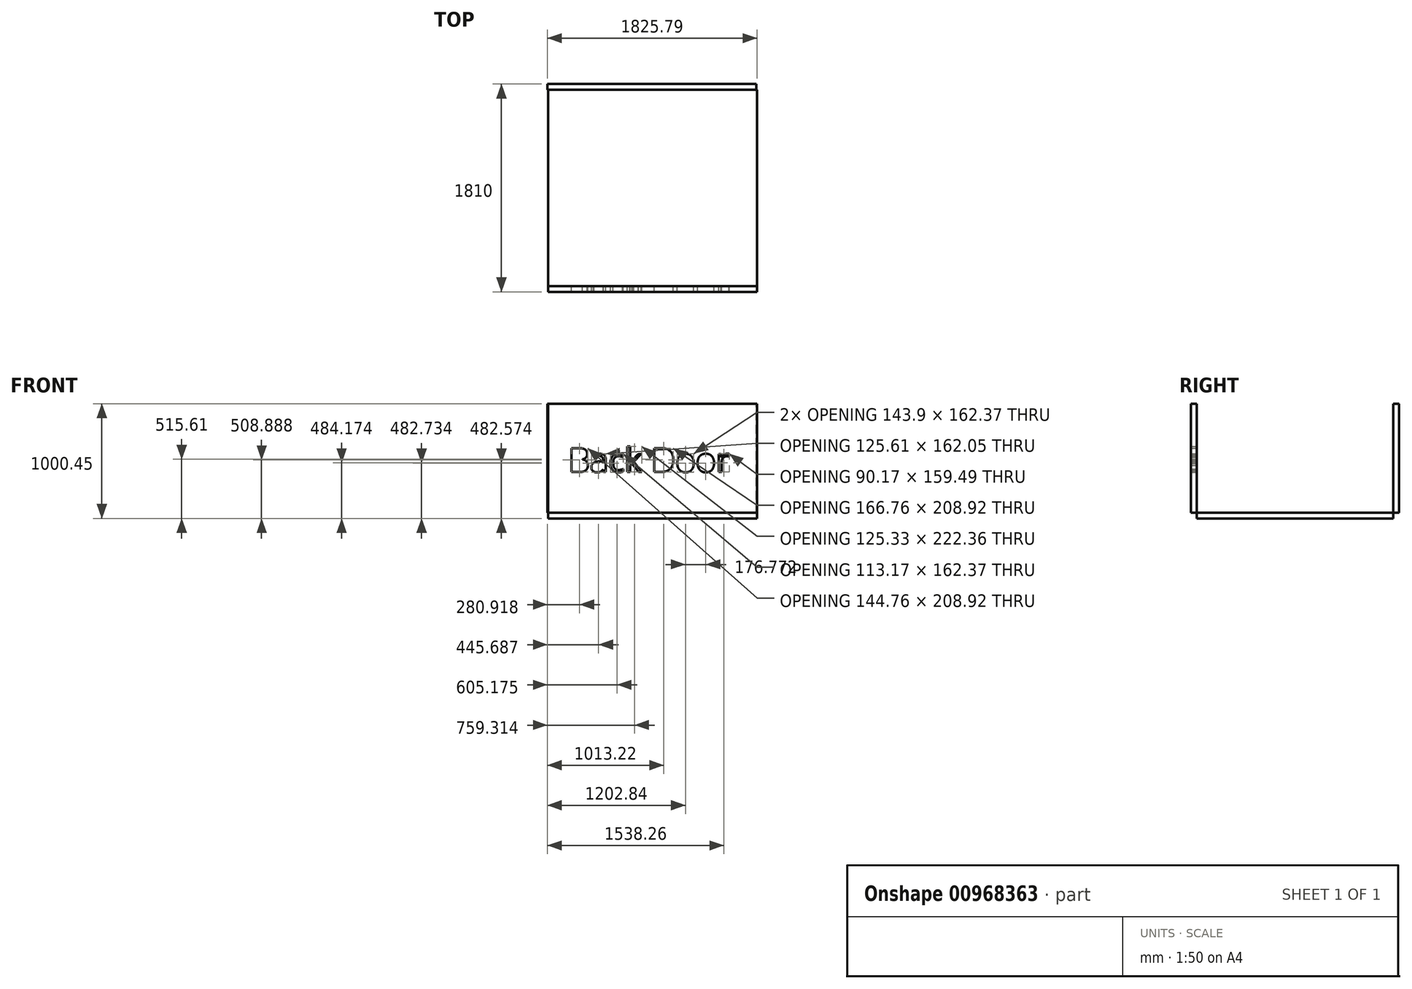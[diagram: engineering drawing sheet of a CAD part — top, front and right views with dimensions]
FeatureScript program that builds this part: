
annotation { "Feature Type Name" : "Feature", "Feature Type Description" : "" }
export const myFeature = defineFeature(function(context is Context, id is Id, definition is map)
    precondition{}
    {
        {
            var Q0;
            Q0=qCreatedBy(makeId("Top.planeOp"),FACE);
            var sketch = newSketch(context, id + "F0", { "sketchPlane" : qUnion([Q0])});
            skLineSegment(sketch, "E0.bottom", {"start": v(-910, 855) * mm, "end": v(910, 855) * mm});
            skLineSegment(sketch, "E0.top", {"start": v(-910, -855) * mm, "end": v(910, -855) * mm});
            skLineSegment(sketch, "E0.left", {"start": v(-910, 855) * mm, "end": v(-910, -855) * mm});
            skLineSegment(sketch, "E0.right", {"start": v(910, 855) * mm, "end": v(910, -855) * mm});
            skPoint(sketch, "E0.middle", {"position": v(0, 0) * mm});
            skSolve(sketch);
        }
        {
            var Q0;
            Q0=makeQuery(id+"F0.imprint","IMPRINT",FACE,{"disambiguationData":[TD([[makeQuery(id+"F0.imprint","IMPRINT",EDGE,{"derivedFrom":sQuery(id+"F0.wireOp",EDGE,"E0.bottom")}),-1.0]])]});
            extrude(context, id + "F1", {"entities" : qUnion([Q0]), "depth" : 50 * mm, "offsetDistance" : 25 * mm});
        }
        {
            var Q0;
            Q0=makeQuery(id+"F1.opExtrude","SWEPT_FACE",FACE,{"disambiguationData":[OSD([sQuery(id+"F0.wireOp",EDGE,"E0.bottom")])]});
            var sketch = newSketch(context, id + "F2", { "sketchPlane" : qUnion([Q0])});
            skLineSegment(sketch, "E1.bottom", {"start": v(-904.21, 50.45) * mm, "end": v(915.79, 50.45) * mm});
            skLineSegment(sketch, "E1.top", {"start": v(-904.21, 1000.45) * mm, "end": v(915.79, 1000.45) * mm});
            skLineSegment(sketch, "E1.left", {"start": v(-904.21, 50.45) * mm, "end": v(-904.21, 1000.45) * mm});
            skLineSegment(sketch, "E1.right", {"start": v(915.79, 50.45) * mm, "end": v(915.79, 1000.45) * mm});
            skSolve(sketch);
        }
        {
            var Q0;
            Q0=makeQuery(id+"F2.imprint","IMPRINT",FACE,{"disambiguationData":[TD([[makeQuery(id+"F2.imprint","IMPRINT",EDGE,{"derivedFrom":sQuery(id+"F2.wireOp",EDGE,"E1.bottom")}),1.0]])]});
            extrude(context, id + "F3", {"entities" : qUnion([Q0]), "depth" : 50 * mm, "offsetDistance" : 25 * mm});
        }
        {
            var Q0;
            Q0=makeQuery(id+"F1.opExtrude","SWEPT_FACE",FACE,{"disambiguationData":[OSD([sQuery(id+"F0.wireOp",EDGE,"E0.top")])]});
            var sketch = newSketch(context, id + "F4", { "sketchPlane" : qUnion([Q0])});
            skLineSegment(sketch, "E2.bottom", {"start": v(-910, 50) * mm, "end": v(910, 50) * mm});
            skLineSegment(sketch, "E2.top", {"start": v(-910, 1000) * mm, "end": v(910, 1000) * mm});
            skLineSegment(sketch, "E2.left", {"start": v(-910, 50) * mm, "end": v(-910, 1000) * mm});
            skLineSegment(sketch, "E2.right", {"start": v(910, 50) * mm, "end": v(910, 1000) * mm});
            skText(sketch, "E3", { "text": "Back Door", "fontName": "OpenSans-Regular.ttf"});
            const initialGuessF4  = {"E3": [-0.73597, 0.40443, 1, 0, 0.2107]};
            skSetInitialGuess(sketch, initialGuessF4);
            skSolve(sketch);
        }
        {
            var Q0;
            Q0=makeQuery(id+"F4.imprint","IMPRINT",FACE,{"disambiguationData":[TD([[makeQuery(id+"F4.imprint","IMPRINT",EDGE,{"derivedFrom":sQuery(id+"F4.wireOp",EDGE,"E2.bottom")}),1.0]])]});
            extrude(context, id + "F5", {"entities" : qUnion([Q0]), "depth" : 50 * mm, "offsetDistance" : 25 * mm});
        }
    });
